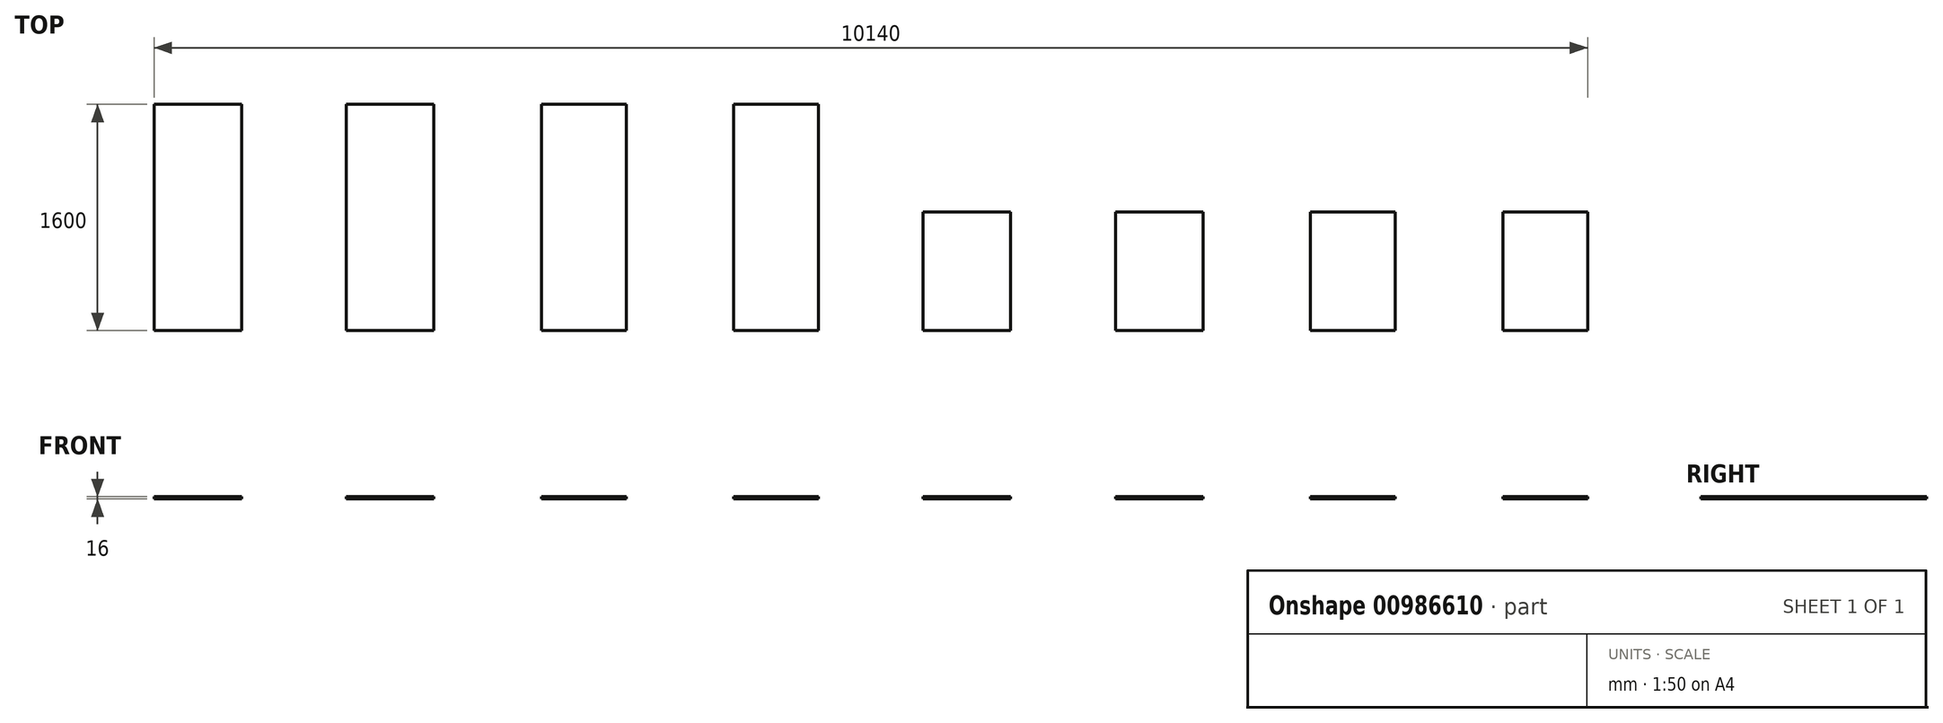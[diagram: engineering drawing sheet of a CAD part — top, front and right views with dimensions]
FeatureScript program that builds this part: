
annotation { "Feature Type Name" : "Feature", "Feature Type Description" : "" }
export const myFeature = defineFeature(function(context is Context, id is Id, definition is map)
    precondition{}
    {
        {
            var Q0;
            Q0=qCreatedBy(makeId("Top.planeOp"),FACE);
            var sketch = newSketch(context, id + "F0", { "sketchPlane" : qUnion([Q0])});
            skLineSegment(sketch, "E0.bottom", {"start": v(0, 0) * mm, "end": v(1000, 0) * mm, "construction": true});
            skLineSegment(sketch, "E0.top", {"start": v(0, 2000) * mm, "end": v(1000, 2000) * mm, "construction": true});
            skLineSegment(sketch, "E0.left", {"start": v(0, 0) * mm, "end": v(0, 2000) * mm, "construction": true});
            skLineSegment(sketch, "E0.right", {"start": v(1000, 0) * mm, "end": v(1000, 2000) * mm, "construction": true});
            skLineSegment(sketch, "E1.0", {"start": v(20, 20) * mm, "end": v(20, 1980) * mm, "construction": true});
            skLineSegment(sketch, "E1.1", {"start": v(20, 20) * mm, "end": v(980, 20) * mm, "construction": true});
            skLineSegment(sketch, "E1.2", {"start": v(980, 20) * mm, "end": v(980, 1980) * mm, "construction": true});
            skLineSegment(sketch, "E1.3", {"start": v(20, 1980) * mm, "end": v(980, 1980) * mm, "construction": true});
            skLineSegment(sketch, "E2.1.0.0", {"start": v(1360, 0) * mm, "end": v(1360, 2000) * mm, "construction": true});
            skLineSegment(sketch, "E2.1.0.1", {"start": v(1380, 20) * mm, "end": v(2340, 20) * mm, "construction": true});
            skLineSegment(sketch, "E2.1.0.2", {"start": v(1380, 1980) * mm, "end": v(2340, 1980) * mm, "construction": true});
            skLineSegment(sketch, "E2.1.0.3", {"start": v(2340, 20) * mm, "end": v(2340, 1980) * mm, "construction": true});
            skLineSegment(sketch, "E2.1.0.4", {"start": v(1360, 0) * mm, "end": v(2360, 0) * mm, "construction": true});
            skLineSegment(sketch, "E2.1.0.5", {"start": v(1380, 20) * mm, "end": v(1380, 1980) * mm, "construction": true});
            skLineSegment(sketch, "E2.1.0.6", {"start": v(1360, 2000) * mm, "end": v(2360, 2000) * mm, "construction": true});
            skLineSegment(sketch, "E2.1.0.7", {"start": v(2360, 0) * mm, "end": v(2360, 2000) * mm, "construction": true});
            skLineSegment(sketch, "E2.2.0.0", {"start": v(2720, 0) * mm, "end": v(2720, 2000) * mm, "construction": true});
            skLineSegment(sketch, "E2.2.0.1", {"start": v(2740, 20) * mm, "end": v(3700, 20) * mm, "construction": true});
            skLineSegment(sketch, "E2.2.0.2", {"start": v(2740, 1980) * mm, "end": v(3700, 1980) * mm, "construction": true});
            skLineSegment(sketch, "E2.2.0.3", {"start": v(3700, 20) * mm, "end": v(3700, 1980) * mm, "construction": true});
            skLineSegment(sketch, "E2.2.0.4", {"start": v(2720, 0) * mm, "end": v(3720, 0) * mm, "construction": true});
            skLineSegment(sketch, "E2.2.0.5", {"start": v(2740, 20) * mm, "end": v(2740, 1980) * mm, "construction": true});
            skLineSegment(sketch, "E2.2.0.6", {"start": v(2720, 2000) * mm, "end": v(3720, 2000) * mm, "construction": true});
            skLineSegment(sketch, "E2.2.0.7", {"start": v(3720, 0) * mm, "end": v(3720, 2000) * mm, "construction": true});
            skLineSegment(sketch, "E2.3.0.0", {"start": v(4080, 0) * mm, "end": v(4080, 2000) * mm, "construction": true});
            skLineSegment(sketch, "E2.3.0.1", {"start": v(4100, 20) * mm, "end": v(5060, 20) * mm, "construction": true});
            skLineSegment(sketch, "E2.3.0.2", {"start": v(4100, 1980) * mm, "end": v(5060, 1980) * mm, "construction": true});
            skLineSegment(sketch, "E2.3.0.3", {"start": v(5060, 20) * mm, "end": v(5060, 1980) * mm, "construction": true});
            skLineSegment(sketch, "E2.3.0.4", {"start": v(4080, 0) * mm, "end": v(5080, 0) * mm, "construction": true});
            skLineSegment(sketch, "E2.3.0.5", {"start": v(4100, 20) * mm, "end": v(4100, 1980) * mm, "construction": true});
            skLineSegment(sketch, "E2.3.0.6", {"start": v(4080, 2000) * mm, "end": v(5080, 2000) * mm, "construction": true});
            skLineSegment(sketch, "E2.3.0.7", {"start": v(5080, 0) * mm, "end": v(5080, 2000) * mm, "construction": true});
            skLineSegment(sketch, "E2.4.0.0", {"start": v(5440, 0) * mm, "end": v(5440, 2000) * mm, "construction": true});
            skLineSegment(sketch, "E2.4.0.1", {"start": v(5460, 20) * mm, "end": v(6420, 20) * mm, "construction": true});
            skLineSegment(sketch, "E2.4.0.2", {"start": v(5460, 1980) * mm, "end": v(6420, 1980) * mm, "construction": true});
            skLineSegment(sketch, "E2.4.0.3", {"start": v(6420, 20) * mm, "end": v(6420, 1980) * mm, "construction": true});
            skLineSegment(sketch, "E2.4.0.4", {"start": v(5440, 0) * mm, "end": v(6440, 0) * mm, "construction": true});
            skLineSegment(sketch, "E2.4.0.5", {"start": v(5460, 20) * mm, "end": v(5460, 1980) * mm, "construction": true});
            skLineSegment(sketch, "E2.4.0.6", {"start": v(5440, 2000) * mm, "end": v(6440, 2000) * mm, "construction": true});
            skLineSegment(sketch, "E2.4.0.7", {"start": v(6440, 0) * mm, "end": v(6440, 2000) * mm, "construction": true});
            skLineSegment(sketch, "E2.direction1", {"start": v(1000, 0) * mm, "end": v(2360, 0) * mm, "construction": true});
            skLineSegment(sketch, "E3.0.5.0", {"start": v(6800, 0) * mm, "end": v(6800, 2000) * mm, "construction": true});
            skLineSegment(sketch, "E3.3.5.0", {"start": v(6820, 20) * mm, "end": v(7780, 20) * mm, "construction": true});
            skLineSegment(sketch, "E3.6.5.0", {"start": v(6820, 1980) * mm, "end": v(7780, 1980) * mm, "construction": true});
            skLineSegment(sketch, "E3.9.5.0", {"start": v(7780, 20) * mm, "end": v(7780, 1980) * mm, "construction": true});
            skLineSegment(sketch, "E3.12.5.0", {"start": v(6800, 0) * mm, "end": v(7800, 0) * mm, "construction": true});
            skLineSegment(sketch, "E3.15.5.0", {"start": v(6820, 20) * mm, "end": v(6820, 1980) * mm, "construction": true});
            skLineSegment(sketch, "E3.18.5.0", {"start": v(6800, 2000) * mm, "end": v(7800, 2000) * mm, "construction": true});
            skLineSegment(sketch, "E3.21.5.0", {"start": v(7800, 0) * mm, "end": v(7800, 2000) * mm, "construction": true});
            skLineSegment(sketch, "E3.0.6.0", {"start": v(8160, 0) * mm, "end": v(8160, 2000) * mm, "construction": true});
            skLineSegment(sketch, "E3.3.6.0", {"start": v(8180, 20) * mm, "end": v(9140, 20) * mm, "construction": true});
            skLineSegment(sketch, "E3.6.6.0", {"start": v(8180, 1980) * mm, "end": v(9140, 1980) * mm, "construction": true});
            skLineSegment(sketch, "E3.9.6.0", {"start": v(9140, 20) * mm, "end": v(9140, 1980) * mm, "construction": true});
            skLineSegment(sketch, "E3.12.6.0", {"start": v(8160, 0) * mm, "end": v(9160, 0) * mm, "construction": true});
            skLineSegment(sketch, "E3.15.6.0", {"start": v(8180, 20) * mm, "end": v(8180, 1980) * mm, "construction": true});
            skLineSegment(sketch, "E3.18.6.0", {"start": v(8160, 2000) * mm, "end": v(9160, 2000) * mm, "construction": true});
            skLineSegment(sketch, "E3.21.6.0", {"start": v(9160, 0) * mm, "end": v(9160, 2000) * mm, "construction": true});
            skLineSegment(sketch, "E3.0.7.0", {"start": v(9520, 0) * mm, "end": v(9520, 2000) * mm, "construction": true});
            skLineSegment(sketch, "E3.3.7.0", {"start": v(9540, 20) * mm, "end": v(10500, 20) * mm, "construction": true});
            skLineSegment(sketch, "E3.6.7.0", {"start": v(9540, 1980) * mm, "end": v(10500, 1980) * mm, "construction": true});
            skLineSegment(sketch, "E3.9.7.0", {"start": v(10500, 20) * mm, "end": v(10500, 1980) * mm, "construction": true});
            skLineSegment(sketch, "E3.12.7.0", {"start": v(9520, 0) * mm, "end": v(10520, 0) * mm, "construction": true});
            skLineSegment(sketch, "E3.15.7.0", {"start": v(9540, 20) * mm, "end": v(9540, 1980) * mm, "construction": true});
            skLineSegment(sketch, "E3.18.7.0", {"start": v(9520, 2000) * mm, "end": v(10520, 2000) * mm, "construction": true});
            skLineSegment(sketch, "E3.21.7.0", {"start": v(10520, 0) * mm, "end": v(10520, 2000) * mm, "construction": true});
            skSolve(sketch);
        }
        {
            var Q0;
            Q0=qCreatedBy(makeId("Top.planeOp"),FACE);
            var sketch = newSketch(context, id + "F1", { "sketchPlane" : qUnion([Q0])});
            skLineSegment(sketch, "E4.bottom", {"start": v(980, 20) * mm, "end": v(360, 20) * mm});
            skLineSegment(sketch, "E4.top", {"start": v(980, 1620) * mm, "end": v(360, 1620) * mm});
            skLineSegment(sketch, "E4.left", {"start": v(980, 20) * mm, "end": v(980, 1620) * mm});
            skLineSegment(sketch, "E4.right", {"start": v(360, 20) * mm, "end": v(360, 1620) * mm});
            skPoint(sketch, "E5", {"position": v(2340, 20) * mm});
            skPoint(sketch, "E6", {"position": v(3700, 20) * mm});
            skPoint(sketch, "E7", {"position": v(5060, 20) * mm});
            skPoint(sketch, "E8", {"position": v(6420, 20) * mm});
            skPoint(sketch, "E9", {"position": v(10500, 20) * mm});
            skPoint(sketch, "E10", {"position": v(9140, 20) * mm});
            skPoint(sketch, "E11", {"position": v(7780, 20) * mm});
            skLineSegment(sketch, "E12.bottom", {"start": v(2340, 20) * mm, "end": v(1720, 20) * mm});
            skLineSegment(sketch, "E12.top", {"start": v(2340, 1620) * mm, "end": v(1720, 1620) * mm});
            skLineSegment(sketch, "E12.left", {"start": v(2340, 20) * mm, "end": v(2340, 1620) * mm});
            skLineSegment(sketch, "E12.right", {"start": v(1720, 20) * mm, "end": v(1720, 1620) * mm});
            skLineSegment(sketch, "E13.bottom", {"start": v(3700, 20) * mm, "end": v(3100, 20) * mm});
            skLineSegment(sketch, "E13.top", {"start": v(3700, 1620) * mm, "end": v(3100, 1620) * mm});
            skLineSegment(sketch, "E13.left", {"start": v(3700, 20) * mm, "end": v(3700, 1620) * mm});
            skLineSegment(sketch, "E13.right", {"start": v(3100, 20) * mm, "end": v(3100, 1620) * mm});
            skLineSegment(sketch, "E14.bottom", {"start": v(5060, 20) * mm, "end": v(4460, 20) * mm});
            skLineSegment(sketch, "E14.top", {"start": v(5060, 1620) * mm, "end": v(4460, 1620) * mm});
            skLineSegment(sketch, "E14.left", {"start": v(5060, 20) * mm, "end": v(5060, 1620) * mm});
            skLineSegment(sketch, "E14.right", {"start": v(4460, 20) * mm, "end": v(4460, 1620) * mm});
            skLineSegment(sketch, "E15.bottom", {"start": v(6420, 20) * mm, "end": v(5800, 20) * mm});
            skLineSegment(sketch, "E15.top", {"start": v(6420, 860) * mm, "end": v(5800, 860) * mm});
            skLineSegment(sketch, "E15.left", {"start": v(6420, 20) * mm, "end": v(6420, 860) * mm});
            skLineSegment(sketch, "E15.right", {"start": v(5800, 20) * mm, "end": v(5800, 860) * mm});
            skLineSegment(sketch, "E16.bottom", {"start": v(7780, 20) * mm, "end": v(7160, 20) * mm});
            skLineSegment(sketch, "E16.top", {"start": v(7780, 860) * mm, "end": v(7160, 860) * mm});
            skLineSegment(sketch, "E16.left", {"start": v(7780, 20) * mm, "end": v(7780, 860) * mm});
            skLineSegment(sketch, "E16.right", {"start": v(7160, 20) * mm, "end": v(7160, 860) * mm});
            skLineSegment(sketch, "E17.bottom", {"start": v(9140, 20) * mm, "end": v(8540, 20) * mm});
            skLineSegment(sketch, "E17.top", {"start": v(9140, 860) * mm, "end": v(8540, 860) * mm});
            skLineSegment(sketch, "E17.left", {"start": v(9140, 20) * mm, "end": v(9140, 860) * mm});
            skLineSegment(sketch, "E17.right", {"start": v(8540, 20) * mm, "end": v(8540, 860) * mm});
            skLineSegment(sketch, "E18.bottom", {"start": v(10500, 20) * mm, "end": v(9900, 20) * mm});
            skLineSegment(sketch, "E18.top", {"start": v(10500, 860) * mm, "end": v(9900, 860) * mm});
            skLineSegment(sketch, "E18.left", {"start": v(10500, 20) * mm, "end": v(10500, 860) * mm});
            skLineSegment(sketch, "E18.right", {"start": v(9900, 20) * mm, "end": v(9900, 860) * mm});
            skSolve(sketch);
        }
        {
            var Q0;
            Q0=qSketchRegion(id+"F1",true);
            extrude(context, id + "F2", {"entities" : qUnion([Q0]), "depth" : 16 * mm, "offsetDistance" : 25 * mm});
        }
    });
